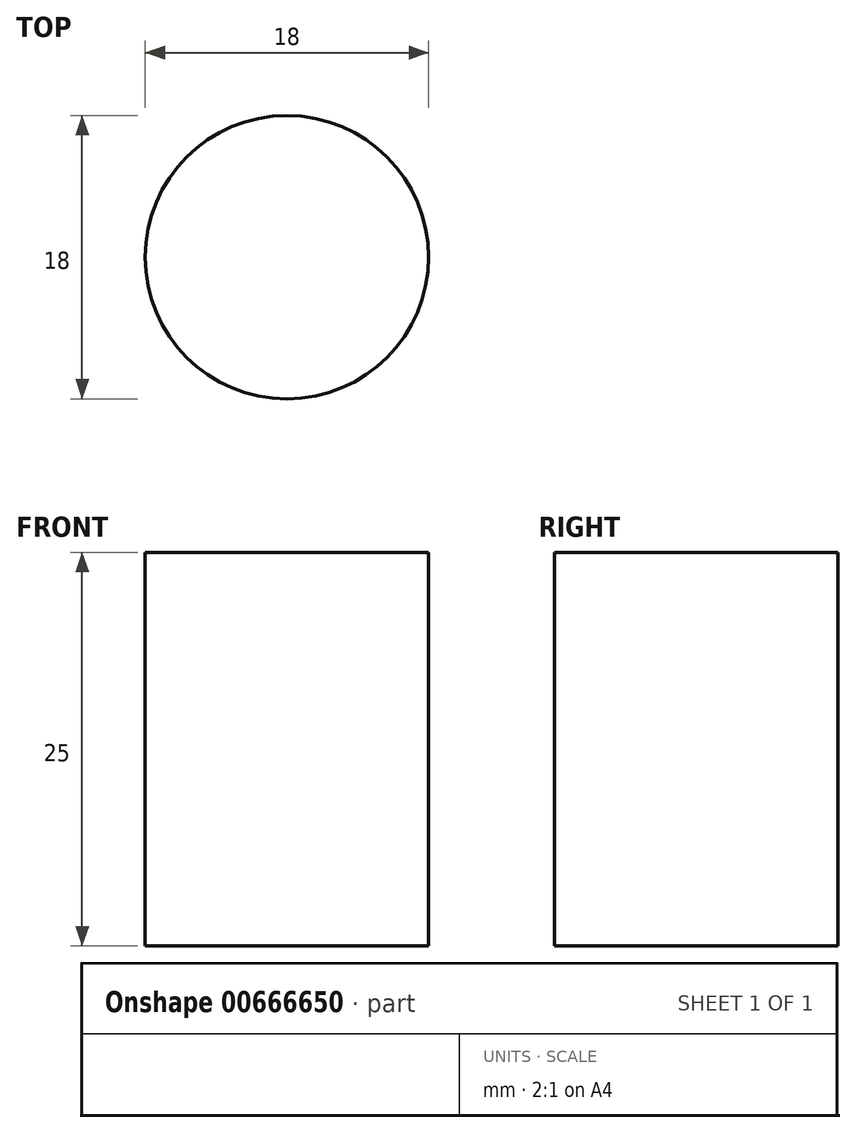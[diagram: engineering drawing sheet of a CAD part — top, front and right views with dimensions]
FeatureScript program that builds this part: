
annotation { "Feature Type Name" : "Feature", "Feature Type Description" : "" }
export const myFeature = defineFeature(function(context is Context, id is Id, definition is map)
    precondition{}
    {
        {
            var Q0;
            Q0=qCreatedBy(makeId("Top.planeOp"),FACE);
            var sketch = newSketch(context, id + "F0", { "sketchPlane" : qUnion([Q0])});
            skCircle(sketch, "E0", {"center": v(0, 0) * mm, "radius": 9 * mm});
            skSolve(sketch);
        }
        {
            var Q0;
            Q0 = qSketchRegion(id + "F0", true);
            extrude(context, id + "F1", {"entities" : qUnion([Q0]), "depth" : 25 * mm, "offsetDistance" : 25 * mm});
        }
    });
